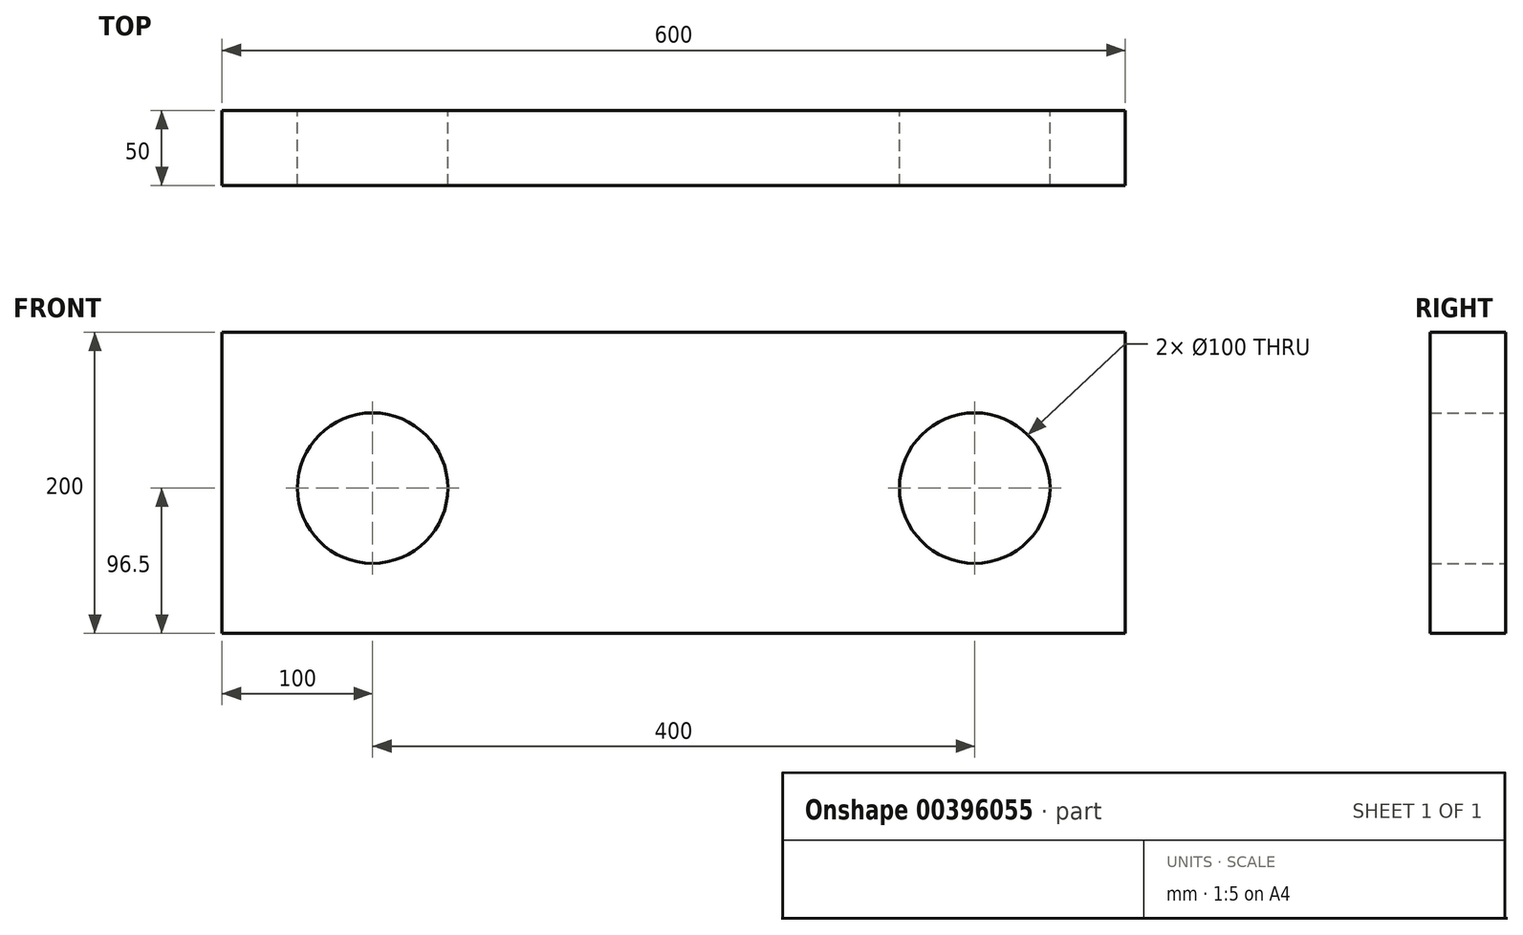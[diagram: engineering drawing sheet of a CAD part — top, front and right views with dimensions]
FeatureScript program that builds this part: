
annotation { "Feature Type Name" : "Feature", "Feature Type Description" : "" }
export const myFeature = defineFeature(function(context is Context, id is Id, definition is map)
    precondition{}
    {
        {
            var Q0;
            Q0=qCreatedBy(makeId("Front.planeOp"),FACE);
            var sketch = newSketch(context, id + "F0", { "sketchPlane" : qUnion([Q0])});
            skLineSegment(sketch, "E0.bottom", {"start": v(-300, 103.5) * mm, "end": v(300, 103.5) * mm});
            skLineSegment(sketch, "E0.top", {"start": v(-300, -96.5) * mm, "end": v(300, -96.5) * mm});
            skLineSegment(sketch, "E0.left", {"start": v(-300, 103.5) * mm, "end": v(-300, -96.5) * mm});
            skLineSegment(sketch, "E0.right", {"start": v(300, 103.5) * mm, "end": v(300, -96.5) * mm});
            skCircle(sketch, "E1", {"center": v(-200, 0) * mm, "radius": 50 * mm});
            skCircle(sketch, "E2", {"center": v(200, 0) * mm, "radius": 50 * mm});
            skSolve(sketch);
        }
        {
            var Q0;
            Q0 = qSketchRegion(id + "F0", true);
            extrude(context, id + "F1", {"entities" : qUnion([Q0]), "depth" : 50 * mm});
        }
    });
